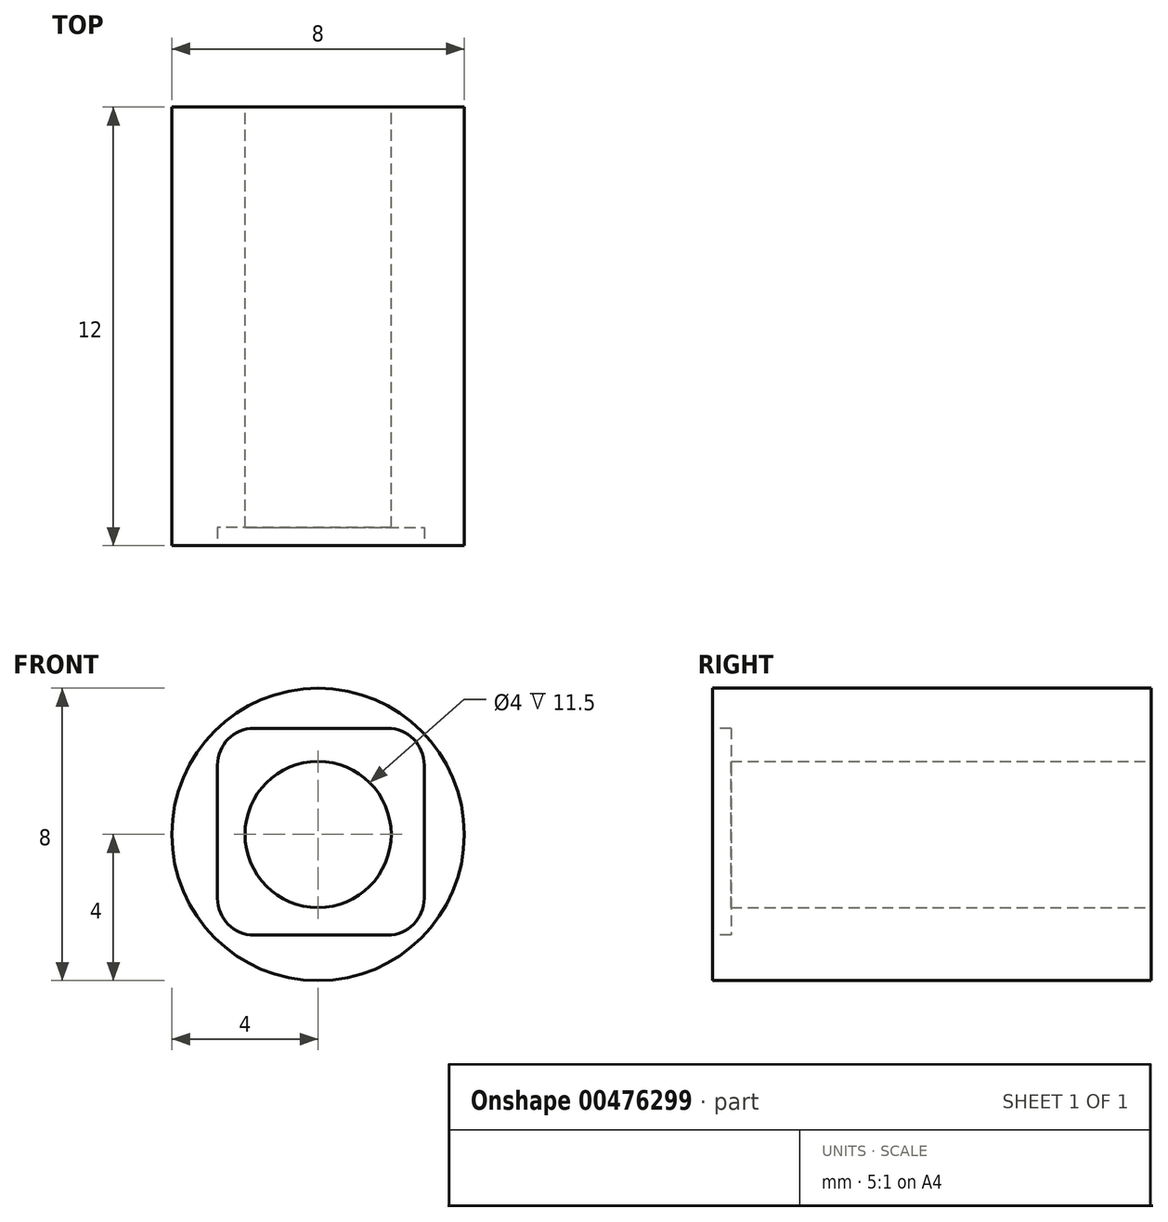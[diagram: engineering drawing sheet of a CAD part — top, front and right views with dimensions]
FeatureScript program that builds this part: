
annotation { "Feature Type Name" : "Feature", "Feature Type Description" : "" }
export const myFeature = defineFeature(function(context is Context, id is Id, definition is map)
    precondition{}
    {
        {
            var Q0;
            Q0=qCreatedBy(makeId("Front.planeOp"),FACE);
            var sketch = newSketch(context, id + "F0", { "sketchPlane" : qUnion([Q0])});
            skCircle(sketch, "E0", {"center": v(0, 0) * mm, "radius": 4 * mm});
            skCircle(sketch, "E1", {"center": v(0, 0) * mm, "radius": 2 * mm});
            skSolve(sketch);
        }
        {
            var Q0;
            Q0=makeQuery(id+"F0.imprint","IMPRINT",FACE,{"disambiguationData":[TD([[makeQuery(id+"F0.imprint","IMPRINT",EDGE,{"derivedFrom":sQuery(id+"F0.wireOp",EDGE,"E0")}),1.0]])]});
            extrude(context, id + "F1", {"entities" : qUnion([Q0]), "depth" : 6 * mm, "hasSecondDirection" : true, "secondDirectionOppositeDirection" : true, "secondDirectionDepth" : 6 * mm});
        }
        {
            var Q0;
            Q0=makeQuery(id+"F1.opExtrude","CAP_FACE",FACE,{"disambiguationData":[OSD([sQuery(id+"F0.wireOp",EDGE,"E0"),sQuery(id+"F0.wireOp",EDGE,"E1")])],"isStart":false});
            var sketch = newSketch(context, id + "F2", { "sketchPlane" : qUnion([Q0])});
            skLineSegment(sketch, "E2.bottom", {"start": v(-1.75, 2.9) * mm, "end": v(1.9, 2.9) * mm});
            skLineSegment(sketch, "E2.top", {"start": v(-1.75, -2.75) * mm, "end": v(1.9, -2.75) * mm});
            skLineSegment(sketch, "E2.left", {"start": v(-2.75, 1.9) * mm, "end": v(-2.75, -1.75) * mm});
            skLineSegment(sketch, "E2.right", {"start": v(2.9, 1.9) * mm, "end": v(2.9, -1.75) * mm});
            skPoint(sketch, "E3.visualSharp", {"position": v(-2.75, 2.9) * mm});
            skArc(sketch, "E3.filletArc", {"start": v(-1.75, 2.9) * mm, "mid": v(-2.46, 2.6) * mm, "end": v(-2.75, 1.9) * mm});
            skPoint(sketch, "E4.visualSharp", {"position": v(-2.75, -2.75) * mm});
            skArc(sketch, "E4.filletArc", {"start": v(-2.75, -1.75) * mm, "mid": v(-2.46, -2.46) * mm, "end": v(-1.75, -2.75) * mm});
            skPoint(sketch, "E5.visualSharp", {"position": v(2.9, 2.9) * mm});
            skArc(sketch, "E5.filletArc", {"start": v(2.9, 1.9) * mm, "mid": v(2.6, 2.6) * mm, "end": v(1.9, 2.9) * mm});
            skPoint(sketch, "E6.visualSharp", {"position": v(2.9, -2.75) * mm});
            skArc(sketch, "E6.filletArc", {"start": v(1.9, -2.75) * mm, "mid": v(2.6, -2.46) * mm, "end": v(2.9, -1.75) * mm});
            skSolve(sketch);
        }
        {
            var Q0;
            Q0=makeQuery(id+"F2.imprint","IMPRINT",FACE,{"disambiguationData":[TD([[makeQuery(id+"F2.imprint","IMPRINT",EDGE,{"derivedFrom":sQuery(id+"F2.wireOp",EDGE,"E2.bottom")}),-1.0]])]});
            extrude(context, id + "F3", {"entities" : qUnion([Q0]), "operationType" : NewBodyOperationType.REMOVE, "oppositeDirection" : true, "depth" : .5 * mm});
        }
    });
